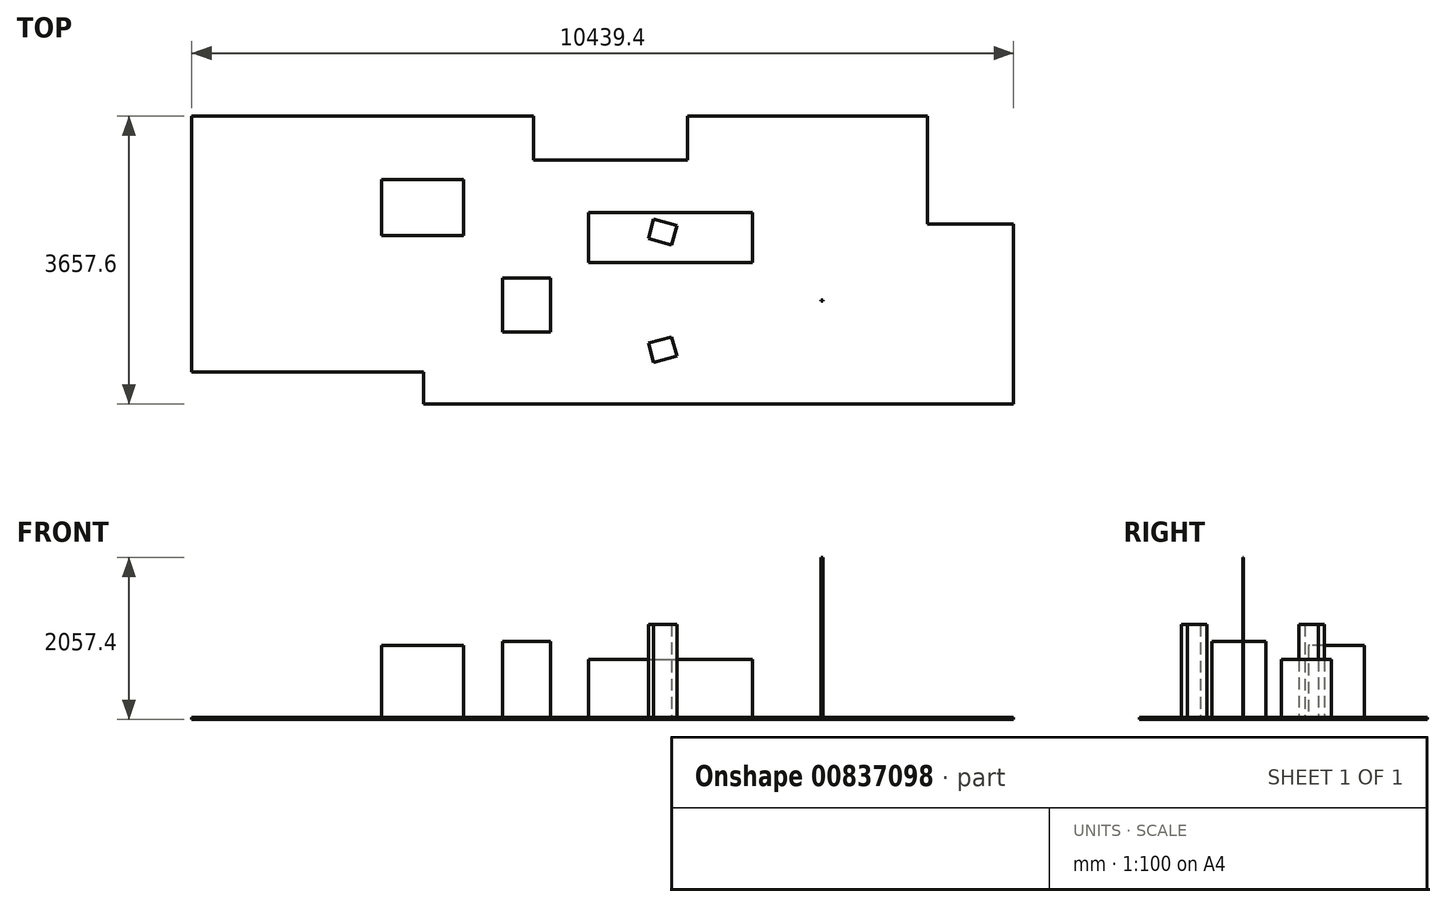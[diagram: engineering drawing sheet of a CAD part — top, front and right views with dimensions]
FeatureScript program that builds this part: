
annotation { "Feature Type Name" : "Feature", "Feature Type Description" : "" }
export const myFeature = defineFeature(function(context is Context, id is Id, definition is map)
    precondition{}
    {
        {
            var Q0;
            Q0=qCreatedBy(makeId("Top.planeOp"),FACE);
            var sketch = newSketch(context, id + "F0", { "sketchPlane" : qUnion([Q0])});
            skLineSegment(sketch, "E0", {"start": v(-1092.2, 0) * mm, "end": v(-4140.2, 0) * mm});
            skLineSegment(sketch, "E1", {"start": v(0, -3657.6) * mm, "end": v(-7493, -3657.6) * mm});
            skLineSegment(sketch, "E2", {"start": v(-7493, -3657.6) * mm, "end": v(-7493, -3251.2) * mm});
            skLineSegment(sketch, "E3", {"start": v(-7493, -3251.2) * mm, "end": v(-10439.4, -3251.2) * mm});
            skLineSegment(sketch, "E4", {"start": v(-4140.2, 0) * mm, "end": v(-4140.2, -558.8) * mm});
            skLineSegment(sketch, "E5", {"start": v(-4140.2, -558.8) * mm, "end": v(-6096, -558.8) * mm});
            skLineSegment(sketch, "E6", {"start": v(-6096, -558.8) * mm, "end": v(-6096, 0) * mm});
            skLineSegment(sketch, "E7", {"start": v(-6096, 0) * mm, "end": v(-10439.4, 0) * mm});
            skLineSegment(sketch, "E8", {"start": v(-10439.4, 0) * mm, "end": v(-10439.4, -3251.2) * mm});
            skLineSegment(sketch, "E9", {"start": v(-939.8, 0) * mm, "end": v(-939.8, -1371.6) * mm, "construction": true});
            skLineSegment(sketch, "E10", {"start": v(-939.8, -1371.6) * mm, "end": v(0, -1371.6) * mm});
            skLineSegment(sketch, "E11", {"start": v(-939.8, -1143) * mm, "end": v(0, -1143) * mm, "construction": true});
            skLineSegment(sketch, "E12", {"start": v(-939.8, -914.4) * mm, "end": v(0, -914.4) * mm, "construction": true});
            skLineSegment(sketch, "E13", {"start": v(-939.8, -685.8) * mm, "end": v(0, -685.8) * mm, "construction": true});
            skLineSegment(sketch, "E14", {"start": v(-939.8, -457.2) * mm, "end": v(0, -457.2) * mm, "construction": true});
            skLineSegment(sketch, "E15", {"start": v(-939.8, -228.6) * mm, "end": v(0, -228.6) * mm, "construction": true});
            skLineSegment(sketch, "E16", {"start": v(-1092.2, 0) * mm, "end": v(-1092.2, -1371.6) * mm});
            skLineSegment(sketch, "E17", {"start": v(-1092.2, -1371.6) * mm, "end": v(-939.8, -1371.6) * mm});
            skLineSegment(sketch, "E18", {"start": v(-10439.4, -2339.52) * mm, "end": v(-10771.83, -1859.13) * mm});
            skLineSegment(sketch, "E19", {"start": v(-1233.09, 0) * mm, "end": v(-1739.67, -290.97) * mm});
            skLineSegment(sketch, "E20.trimOffspring", {"start": v(0, -1371.6) * mm, "end": v(0, -3657.6) * mm});
            skSolve(sketch);
        }
        {
            var Q0;
            Q0 = qSketchRegion(id + "F0", true);
            extrude(context, id + "F1", {"entities" : qUnion([Q0]), "oppositeDirection" : true, "depth" : 25.4 * mm, "offsetDistance" : 25.4 * mm});
        }
        {
            var Q0;
            Q0=qCreatedBy(makeId("Top.planeOp"),FACE);
            var sketch = newSketch(context, id + "F2", { "sketchPlane" : qUnion([Q0])});
            skLineSegment(sketch, "E21.bottom", {"start": v(-5403.63, -1225) * mm, "end": v(-3320.83, -1225) * mm});
            skLineSegment(sketch, "E21.top", {"start": v(-5403.63, -1860) * mm, "end": v(-3320.83, -1860) * mm});
            skLineSegment(sketch, "E21.left", {"start": v(-5403.63, -1225) * mm, "end": v(-5403.63, -1860) * mm});
            skLineSegment(sketch, "E21.right", {"start": v(-3320.83, -1225) * mm, "end": v(-3320.83, -1860) * mm});
            skSolve(sketch);
        }
        {
            var Q0;
            Q0 = qSketchRegion(id + "F2", true);
            extrude(context, id + "F3", {"entities" : qUnion([Q0]), "depth" : 736.6 * mm, "offsetDistance" : 25.4 * mm});
        }
        {
            var Q0;
            Q0=qCreatedBy(makeId("Top.planeOp"),FACE);
            var sketch = newSketch(context, id + "F4", { "sketchPlane" : qUnion([Q0])});
            skLineSegment(sketch, "E22.bottom", {"start": v(-8030.64, -806.09) * mm, "end": v(-6989.24, -806.09) * mm});
            skLineSegment(sketch, "E22.top", {"start": v(-8030.64, -1517.29) * mm, "end": v(-6989.24, -1517.29) * mm});
            skLineSegment(sketch, "E22.left", {"start": v(-8030.64, -806.09) * mm, "end": v(-8030.64, -1517.29) * mm});
            skLineSegment(sketch, "E22.right", {"start": v(-6989.24, -806.09) * mm, "end": v(-6989.24, -1517.29) * mm});
            skSolve(sketch);
        }
        {
            var Q0;
            Q0 = qSketchRegion(id + "F4", true);
            extrude(context, id + "F5", {"entities" : qUnion([Q0]), "depth" : 914.4 * mm, "offsetDistance" : 25.4 * mm});
        }
        {
            var Q0;
            Q0=qCreatedBy(makeId("Top.planeOp"),FACE);
            var sketch = newSketch(context, id + "F6", { "sketchPlane" : qUnion([Q0])});
            skLineSegment(sketch, "E23.bottom", {"start": v(-6495.38, -2054.98) * mm, "end": v(-5885.78, -2054.98) * mm});
            skLineSegment(sketch, "E23.top", {"start": v(-6495.38, -2740.78) * mm, "end": v(-5885.78, -2740.78) * mm});
            skLineSegment(sketch, "E23.left", {"start": v(-6495.38, -2054.98) * mm, "end": v(-6495.38, -2740.78) * mm});
            skLineSegment(sketch, "E23.right", {"start": v(-5885.78, -2054.98) * mm, "end": v(-5885.78, -2740.78) * mm});
            skSolve(sketch);
        }
        {
            var Q0;
            Q0 = qSketchRegion(id + "F6", true);
            extrude(context, id + "F7", {"entities" : qUnion([Q0]), "depth" : 965.2 * mm, "offsetDistance" : 25.4 * mm});
        }
        {
            var Q0;
            Q0=makeQuery(id+"F0.imprint","IMPRINT",FACE,{"disambiguationData":[TD([[makeQuery(id+"F0.imprint","IMPRINT",EDGE,{"derivedFrom":sQuery(id+"F0.wireOp",EDGE,"E1")}),-1.0]])]});
            var sketch = newSketch(context, id + "F8", { "sketchPlane" : qUnion([Q0])});
            skLineSegment(sketch, "E24.bottom", {"start": v(-4638.26, -2882.48) * mm, "end": v(-4343.84, -2803.6) * mm});
            skLineSegment(sketch, "E24.top", {"start": v(-4572.52, -3127.82) * mm, "end": v(-4278.1, -3048.94) * mm});
            skLineSegment(sketch, "E24.left", {"start": v(-4638.26, -2882.48) * mm, "end": v(-4572.52, -3127.82) * mm});
            skLineSegment(sketch, "E24.right", {"start": v(-4343.84, -2803.6) * mm, "end": v(-4278.1, -3048.94) * mm});
            skLineSegment(sketch, "E25", {"start": v(-5101.85, -2219.4) * mm, "end": v(-3675.17, -2219.4) * mm, "construction": true});
            skLineSegment(sketch, "E26.MirrorCS", {"start": v(-4572.52, -1310.96) * mm, "end": v(-4278.1, -1389.85) * mm});
            skLineSegment(sketch, "E27.MirrorCS", {"start": v(-4638.26, -1556.3) * mm, "end": v(-4343.84, -1635.2) * mm});
            skLineSegment(sketch, "E28.MirrorCS", {"start": v(-4343.84, -1635.2) * mm, "end": v(-4278.1, -1389.85) * mm});
            skLineSegment(sketch, "E29.MirrorCS", {"start": v(-4638.26, -1556.3) * mm, "end": v(-4572.52, -1310.96) * mm});
            skSolve(sketch);
        }
        {
            var Q0;
            Q0 = qSketchRegion(id + "F8", true);
            extrude(context, id + "F9", {"entities" : qUnion([Q0]), "depth" : 1181.1 * mm, "offsetDistance" : 25.4 * mm});
        }
        {
            var Q0;
            Q0=makeQuery(id+"F8.imprint","IMPRINT",FACE,{"disambiguationData":[TD([[makeQuery(id+"F8.imprint","IMPRINT",EDGE,{"derivedFrom":sQuery(id+"F8.wireOp",EDGE,"E24.bottom")}),1.0]])]});
            var sketch = newSketch(context, id + "F10", { "sketchPlane" : qUnion([Q0])});
            skLineSegment(sketch, "E30.bottom", {"start": v(-2444.88, -2337.5) * mm, "end": v(-2421.14, -2337.5) * mm});
            skLineSegment(sketch, "E30.top", {"start": v(-2444.88, -2348.67) * mm, "end": v(-2421.14, -2348.67) * mm});
            skLineSegment(sketch, "E30.left", {"start": v(-2444.88, -2337.5) * mm, "end": v(-2444.88, -2348.67) * mm});
            skLineSegment(sketch, "E30.right", {"start": v(-2421.14, -2337.5) * mm, "end": v(-2421.14, -2348.67) * mm});
            skSolve(sketch);
        }
        {
            var Q0;
            Q0 = qSketchRegion(id + "F10", true);
            extrude(context, id + "F11", {"entities" : qUnion([Q0]), "depth" : 2032 * mm, "offsetDistance" : 25.4 * mm});
        }
    });
